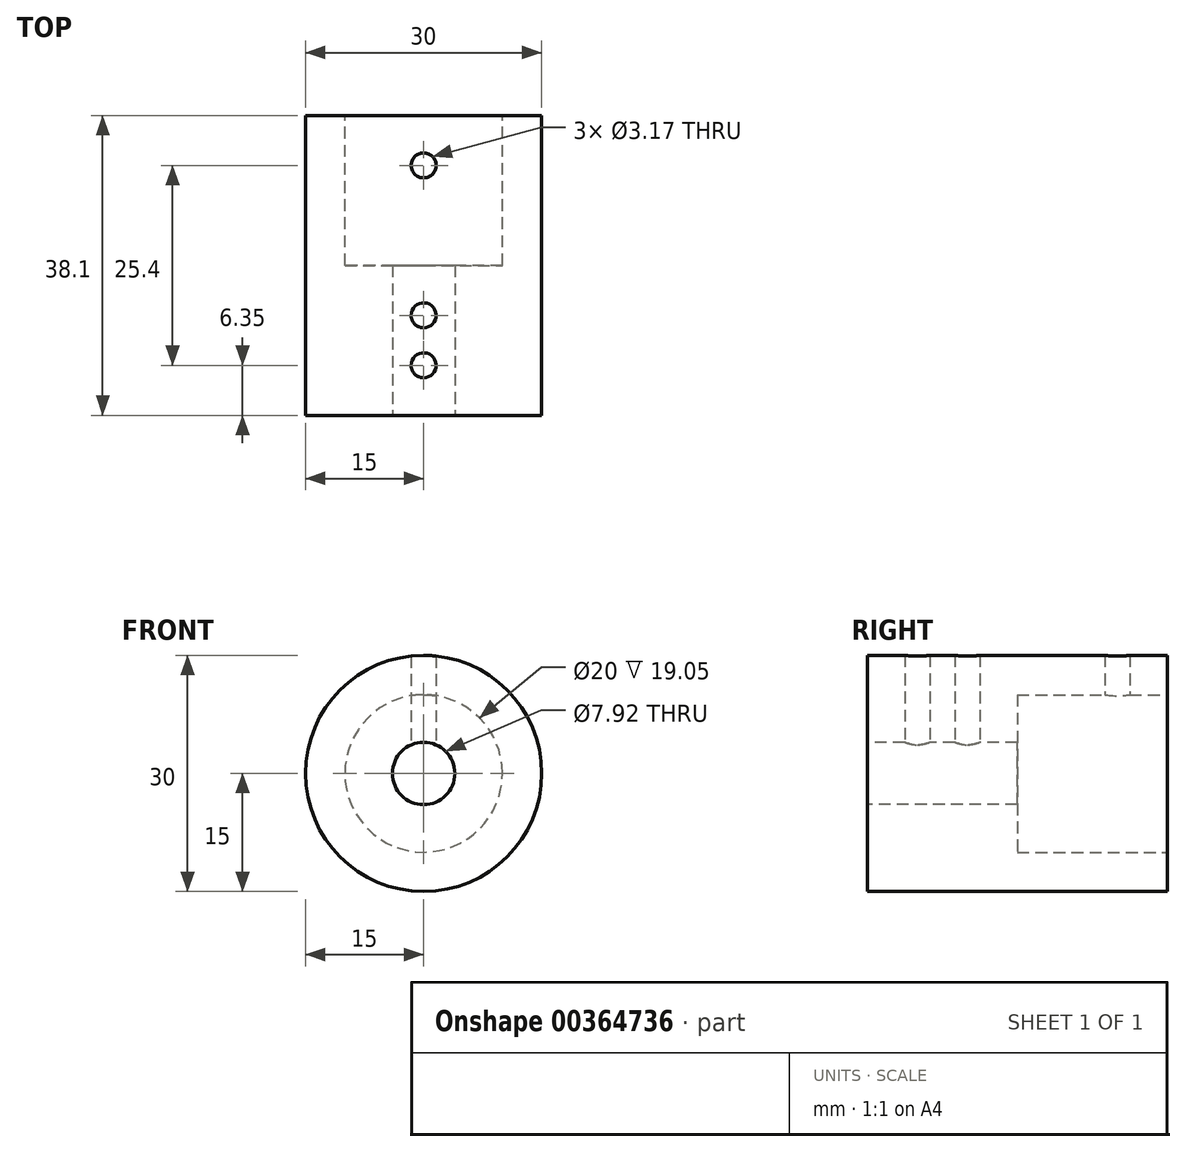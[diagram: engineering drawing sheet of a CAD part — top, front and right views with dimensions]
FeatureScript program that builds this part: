
annotation { "Feature Type Name" : "Feature", "Feature Type Description" : "" }
export const myFeature = defineFeature(function(context is Context, id is Id, definition is map)
    precondition{}
    {
        {
            var Q0;
            Q0=qCreatedBy(makeId("Front.planeOp"),FACE);
            var sketch = newSketch(context, id + "F0", { "sketchPlane" : qUnion([Q0])});
            skCircle(sketch, "E0", {"center": v(0, 0) * mm, "radius": 15 * mm});
            skSolve(sketch);
        }
        {
            var Q0;
            Q0 = qSketchRegion(id + "F0", true);
            extrude(context, id + "F1", {"entities" : qUnion([Q0]), "depth" : 38.1 * mm});
        }
        {
            var Q0;
            Q0=makeQuery(id+"F1.opExtrude","CAP_FACE",FACE,{"disambiguationData":[OSD([sQuery(id+"F0.wireOp",EDGE,"E0")])],"isStart":true});
            var sketch = newSketch(context, id + "F2", { "sketchPlane" : qUnion([Q0])});
            skCircle(sketch, "E1", {"center": v(0, 0) * mm, "radius": 10 * mm});
            skSolve(sketch);
        }
        {
            var Q0;
            Q0 = qSketchRegion(id + "F2", true);
            extrude(context, id + "F3", {"entities" : qUnion([Q0]), "operationType" : NewBodyOperationType.REMOVE, "oppositeDirection" : true, "depth" : 19.05 * mm});
        }
        {
            var Q0;
            Q0=makeQuery(id+"F1.opExtrude","CAP_FACE",FACE,{"disambiguationData":[OSD([sQuery(id+"F0.wireOp",EDGE,"E0")])],"isStart":false});
            var sketch = newSketch(context, id + "F4", { "sketchPlane" : qUnion([Q0])});
            skCircle(sketch, "E2", {"center": v(0, 0) * mm, "radius": 3.96 * mm});
            skSolve(sketch);
        }
        {
            var Q0;
            Q0 = qSketchRegion(id + "F4", true);
            extrude(context, id + "F5", {"entities" : qUnion([Q0]), "operationType" : NewBodyOperationType.REMOVE, "oppositeDirection" : true, "depth" : 19.05 * mm});
        }
        {
            var Q0;
            Q0=qCreatedBy(makeId("Top.planeOp"),FACE);
            var sketch = newSketch(context, id + "F6", { "sketchPlane" : qUnion([Q0])});
            skCircle(sketch, "E3", {"center": v(0, -31.75) * mm, "radius": 1.59 * mm});
            skCircle(sketch, "E4", {"center": v(0, -25.4) * mm, "radius": 1.59 * mm});
            skCircle(sketch, "E5", {"center": v(0, -6.35) * mm, "radius": 1.59 * mm});
            skSolve(sketch);
        }
        {
            var Q0;
            Q0 = qSketchRegion(id + "F6", true);
            extrude(context, id + "F7", {"entities" : qUnion([Q0]), "operationType" : NewBodyOperationType.REMOVE, "depth" : 25.4 * mm});
        }
    });
